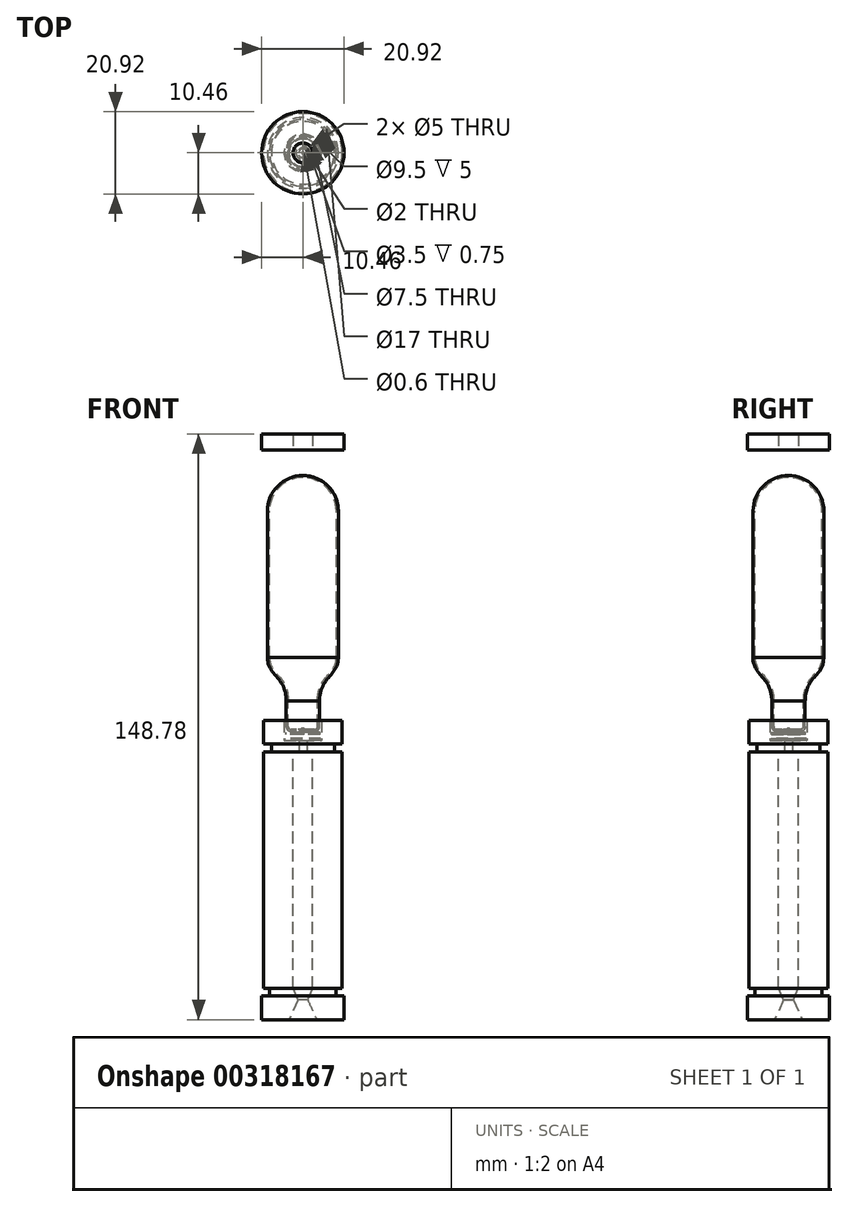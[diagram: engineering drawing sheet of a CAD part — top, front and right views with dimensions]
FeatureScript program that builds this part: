
annotation { "Feature Type Name" : "Feature", "Feature Type Description" : "" }
export const myFeature = defineFeature(function(context is Context, id is Id, definition is map)
    precondition{}
    {
        {
            var Q0;
            Q0=qCreatedBy(makeId("Front.planeOp"),FACE);
            var sketch = newSketch(context, id + "F0", { "sketchPlane" : qUnion([Q0])});
            skLineSegment(sketch, "E0", {"start": v(9, 56.25) * mm, "end": v(9, 19) * mm});
            skLineSegment(sketch, "E1", {"start": v(0, 0) * mm, "end": v(2.25, 0) * mm});
            skLineSegment(sketch, "E2", {"start": v(2.25, 0) * mm, "end": v(2.25, 0.25) * mm});
            skFitSpline(sketch, "E3", {"points": [v(4.25, 8) * mm, v(9, 19) * mm], "startDerivative": vector(0, 18.73) * mm, "endDerivative": vector(0, 14.27) * mm});
            skArc(sketch, "E4", {"start": v(9, 56.25) * mm, "mid": v(6.36, 62.61) * mm, "end": v(0, 65.25) * mm});
            skLineSegment(sketch, "E5", {"start": v(0, 0) * mm, "end": v(0, 65.25) * mm, "construction": true});
            skLineSegment(sketch, "E6", {"start": v(2.25, 0.25) * mm, "end": v(4.25, 0.25) * mm});
            skLineSegment(sketch, "E7", {"start": v(4.25, 0.25) * mm, "end": v(4.25, 8) * mm});
            skLineSegment(sketch, "E8", {"start": v(0, 65.25) * mm, "end": v(0, 0) * mm});
            skSolve(sketch);
        }
        {
            var Q0;
            Q0 = qSketchRegion(id + "F0", true);
            var Q1;
            Q1=sQuery(id+"F0.wireOp",EDGE,"E8");
            revolve(context, id + "F1", {"surfaceOperationType" : NewSurfaceOperationType.NEW, "entities" : qUnion([Q0]), "axis" : qUnion([Q1]), "revolveType" : RevolveType.FULL});
        }
        {
            var Q0;
            Q0=makeQuery(id+"F1.opRevolve","SWEPT_EDGE",EDGE,{"disambiguationData":[OSD([sQuery(id+"F0.wireOp",EDGE,"E6"),sQuery(id+"F0.wireOp",EDGE,"E7")])]});
            fillet(context, id + "F2", {"entities" : qUnion([Q0]), "radius" : 1.25 * mm, "allowEdgeOverflow" : false});
        }
        {
            var Q0;
            Q0=makeQuery(id+"F1.opRevolve","SWEPT_FACE",FACE,{"disambiguationData":[OSD([sQuery(id+"F0.wireOp",EDGE,"E1")])]});
            shell(context, id + "F3", {"entities" : qUnion([Q0]), "thickness" : .5 * mm});
        }
        {
            var Q0;
            Q0=qCreatedBy(makeId("Front.planeOp"),FACE);
            var sketch = newSketch(context, id + "F4", { "sketchPlane" : qUnion([Q0])});
            skLineSegment(sketch, "E9", {"start": v(4.75, 3) * mm, "end": v(4.75, -2) * mm});
            skLineSegment(sketch, "E10", {"start": v(4.75, -2) * mm, "end": v(1, -2) * mm});
            skLineSegment(sketch, "E11", {"start": v(4.75, 3) * mm, "end": v(10, 3) * mm});
            skLineSegment(sketch, "E12", {"start": v(10, 3) * mm, "end": v(10, -3) * mm});
            skLineSegment(sketch, "E13", {"start": v(10, -3) * mm, "end": v(8, -3) * mm});
            skLineSegment(sketch, "E14", {"start": v(8, -3) * mm, "end": v(8, -5) * mm});
            skLineSegment(sketch, "E15", {"start": v(8, -5) * mm, "end": v(1, -5) * mm});
            skLineSegment(sketch, "E16", {"start": v(1, -5) * mm, "end": v(1, -2) * mm});
            skLineSegment(sketch, "E17", {"start": v(0, -15.13) * mm, "end": v(0, 8.9) * mm, "construction": true});
            skSolve(sketch);
        }
        {
            var Q0;
            Q0 = qSketchRegion(id + "F4", true);
            var Q1;
            Q1=sQuery(id+"F4.wireOp",EDGE,"E17");
            revolve(context, id + "F5", {"surfaceOperationType" : NewSurfaceOperationType.NEW, "entities" : qUnion([Q0]), "axis" : qUnion([Q1]), "revolveType" : RevolveType.FULL});
        }
        {
            var Q0;
            Q0=qCreatedBy(makeId("Front.planeOp"),FACE);
            var sketch = newSketch(context, id + "F6", { "sketchPlane" : qUnion([Q0])});
            skLineSegment(sketch, "E18.bottom", {"start": v(2.5, -5) * mm, "end": v(10, -5) * mm});
            skLineSegment(sketch, "E18.top", {"start": v(2.5, -65) * mm, "end": v(10, -65) * mm});
            skLineSegment(sketch, "E18.left", {"start": v(2.5, -5) * mm, "end": v(2.5, -65) * mm});
            skLineSegment(sketch, "E18.right", {"start": v(10, -5) * mm, "end": v(10, -65) * mm});
            skLineSegment(sketch, "E19", {"start": v(0, -9.07) * mm, "end": v(0, -53.46) * mm, "construction": true});
            skSolve(sketch);
        }
        {
            var Q0;
            Q0 = qSketchRegion(id + "F6", true);
            var Q1;
            Q1=sQuery(id+"F6.wireOp",EDGE,"E19");
            revolve(context, id + "F7", {"surfaceOperationType" : NewSurfaceOperationType.NEW, "entities" : qUnion([Q0]), "axis" : qUnion([Q1]), "revolveType" : RevolveType.FULL});
        }
        {
            var Q0;
            Q0=qCreatedBy(makeId("Front.planeOp"),FACE);
            var sketch = newSketch(context, id + "F8", { "sketchPlane" : qUnion([Q0])});
            skLineSegment(sketch, "E20", {"start": v(0, -16.65) * mm, "end": v(0, -67.34) * mm, "construction": true});
            skLineSegment(sketch, "E21", {"start": v(2.5, -65) * mm, "end": v(8.46, -65) * mm});
            skLineSegment(sketch, "E22", {"start": v(8.46, -65) * mm, "end": v(8.46, -67) * mm});
            skLineSegment(sketch, "E23", {"start": v(8.46, -67) * mm, "end": v(10.46, -67) * mm});
            skLineSegment(sketch, "E24", {"start": v(10.46, -67) * mm, "end": v(10.46, -73) * mm});
            skLineSegment(sketch, "E25", {"start": v(10.46, -73) * mm, "end": v(3.5, -73) * mm});
            skLineSegment(sketch, "E26", {"start": v(2.5, -65) * mm, "end": v(1.25, -68) * mm});
            skLineSegment(sketch, "E27", {"start": v(1.25, -68) * mm, "end": v(3.5, -73) * mm});
            skSolve(sketch);
        }
        {
            var Q0;
            Q0 = qSketchRegion(id + "F8", true);
            var Q1;
            Q1=sQuery(id+"F8.wireOp",EDGE,"E20");
            revolve(context, id + "F9", {"surfaceOperationType" : NewSurfaceOperationType.NEW, "entities" : qUnion([Q0]), "axis" : qUnion([Q1]), "revolveType" : RevolveType.FULL});
        }
        {
            var Q0;
            Q0=qCreatedBy(makeId("Front.planeOp"),FACE);
            var sketch = newSketch(context, id + "F10", { "sketchPlane" : qUnion([Q0])});
            skLineSegment(sketch, "E28", {"start": v(0, 60.84) * mm, "end": v(0, 79.86) * mm, "construction": true});
            skLineSegment(sketch, "E29.bottom", {"start": v(0, 75.78) * mm, "end": v(10.46, 75.78) * mm});
            skLineSegment(sketch, "E29.top", {"start": v(0, 71.77) * mm, "end": v(10.46, 71.77) * mm});
            skLineSegment(sketch, "E29.left", {"start": v(0, 75.78) * mm, "end": v(0, 71.77) * mm});
            skLineSegment(sketch, "E29.right", {"start": v(10.46, 75.78) * mm, "end": v(10.46, 71.77) * mm});
            skSolve(sketch);
        }
        {
            var Q0;
            Q0 = qSketchRegion(id + "F10", true);
            var Q1;
            Q1=sQuery(id+"F10.wireOp",EDGE,"E28");
            revolve(context, id + "F11", {"surfaceOperationType" : NewSurfaceOperationType.NEW, "entities" : qUnion([Q0]), "axis" : qUnion([Q1]), "revolveType" : RevolveType.FULL});
        }
        {
            var Q0;
            Q0=makeQuery(id+"F11.opRevolve","SWEPT_FACE",FACE,{"disambiguationData":[OSD([sQuery(id+"F10.wireOp",EDGE,"E29.bottom")])]});
            var sketch = newSketch(context, id + "F12", { "sketchPlane" : qUnion([Q0])});
            skPoint(sketch, "E30", {"position": v(0, 0) * mm});
            skSolve(sketch);
        }
        {
            var Q0;
            Q0=sQuery(id+"F12.wireOp",VERTEX,"E30");
            var Q1;
            Q1=makeQuery(id+"F11.opRevolve","SWEPT_BODY",BODY,{"disambiguationData":[OSD([sQuery(id+"F10.wireOp",EDGE,"E29.bottom"),sQuery(id+"F10.wireOp",EDGE,"E29.top"),sQuery(id+"F10.wireOp",EDGE,"E29.left"),sQuery(id+"F10.wireOp",EDGE,"E29.right")])]});
            hole(context, id + "F13", {"style" : HoleStyle.SIMPLE, "endStyle" : HoleEndStyle.THROUGH, "holeDiameter" : 5 * mm, "majorDiameter" : 5 * mm, "isTappedThrough" : true, "tappedDepth" : 12 * mm, "tapClearance" : 3, "locations" : qUnion([Q0]), "scope" : qUnion([Q1])});
        }
        {
            var Q0;
            Q0=qCreatedBy(makeId("Front.planeOp"),FACE);
            var sketch = newSketch(context, id + "F14", { "sketchPlane" : qUnion([Q0])});
            skLineSegment(sketch, "E31.bottom", {"start": v(0, -1.5) * mm, "end": v(4.5, -1.5) * mm});
            skLineSegment(sketch, "E31.top", {"start": v(0, -2) * mm, "end": v(4.5, -2) * mm});
            skLineSegment(sketch, "E31.left", {"start": v(0, -1.5) * mm, "end": v(0, -2) * mm});
            skLineSegment(sketch, "E31.right", {"start": v(4.5, -1.5) * mm, "end": v(4.5, -2) * mm});
            skLineSegment(sketch, "E32", {"start": v(0, 0) * mm, "end": v(0, -3.49) * mm, "construction": true});
            skSolve(sketch);
        }
        {
            var Q0;
            Q0=makeQuery(id+"F14.imprint","IMPRINT",FACE,{"disambiguationData":[TD([[makeQuery(id+"F14.imprint","IMPRINT",EDGE,{"derivedFrom":sQuery(id+"F14.wireOp",EDGE,"E31.bottom")}),-1.0]])]});
            var Q1;
            Q1=sQuery(id+"F14.wireOp",EDGE,"E32");
            revolve(context, id + "F15", {"surfaceOperationType" : NewSurfaceOperationType.NEW, "entities" : qUnion([Q0]), "axis" : qUnion([Q1]), "revolveType" : RevolveType.FULL});
        }
        {
            var Q0;
            Q0=qCreatedBy(makeId("Front.planeOp"),FACE);
            var sketch = newSketch(context, id + "F16", { "sketchPlane" : qUnion([Q0])});
            skLineSegment(sketch, "E33", {"start": v(0, 5.47) * mm, "end": v(0, -2.97) * mm, "construction": true});
            skLineSegment(sketch, "E34", {"start": v(0.3, 1) * mm, "end": v(0.3, -0.5) * mm});
            skLineSegment(sketch, "E35", {"start": v(0.3, -0.5) * mm, "end": v(4.3, -0.5) * mm});
            skLineSegment(sketch, "E36", {"start": v(4.3, -0.5) * mm, "end": v(4.3, 0) * mm});
            skLineSegment(sketch, "E37", {"start": v(4.3, 0) * mm, "end": v(1.2, 0) * mm});
            skLineSegment(sketch, "E38", {"start": v(0.3, 1) * mm, "end": v(1.2, 0) * mm});
            skSolve(sketch);
        }
        {
            var Q0;
            Q0=makeQuery(id+"F16.imprint","IMPRINT",FACE,{"disambiguationData":[TD([[makeQuery(id+"F16.imprint","IMPRINT",EDGE,{"derivedFrom":sQuery(id+"F16.wireOp",EDGE,"E34")}),1.0]])]});
            var Q1;
            Q1=sQuery(id+"F16.wireOp",EDGE,"E33");
            revolve(context, id + "F17", {"surfaceOperationType" : NewSurfaceOperationType.NEW, "entities" : qUnion([Q0]), "axis" : qUnion([Q1]), "revolveType" : RevolveType.FULL});
        }
    });
